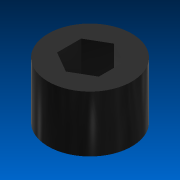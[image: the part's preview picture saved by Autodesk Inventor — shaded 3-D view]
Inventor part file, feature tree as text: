
AUTODESK INVENTOR PART (.ipt)
format: ipt  version: 2022.2 (Build 262287000, 287)  size: 96,768 bytes
history: native  units: in
note: dims shown in document units (in); Inventor stores cm internally (conversion verified against a paired STEP export)
features: extrude x1, sketch x1
ambient origin geometry x8: Origin, YZ Plane, XZ Plane, XY Plane, X Axis, Y Axis, Z Axis, Center Point
bodies: Solid1 (feature_tree)
feature tree (2):
  extrude  "Extrusion1"  Depth=0.3363in
  sketch  "Sketch1"  dims[d0=0.25in d1=0.5in d2=0.3363in d3=0.0in]
